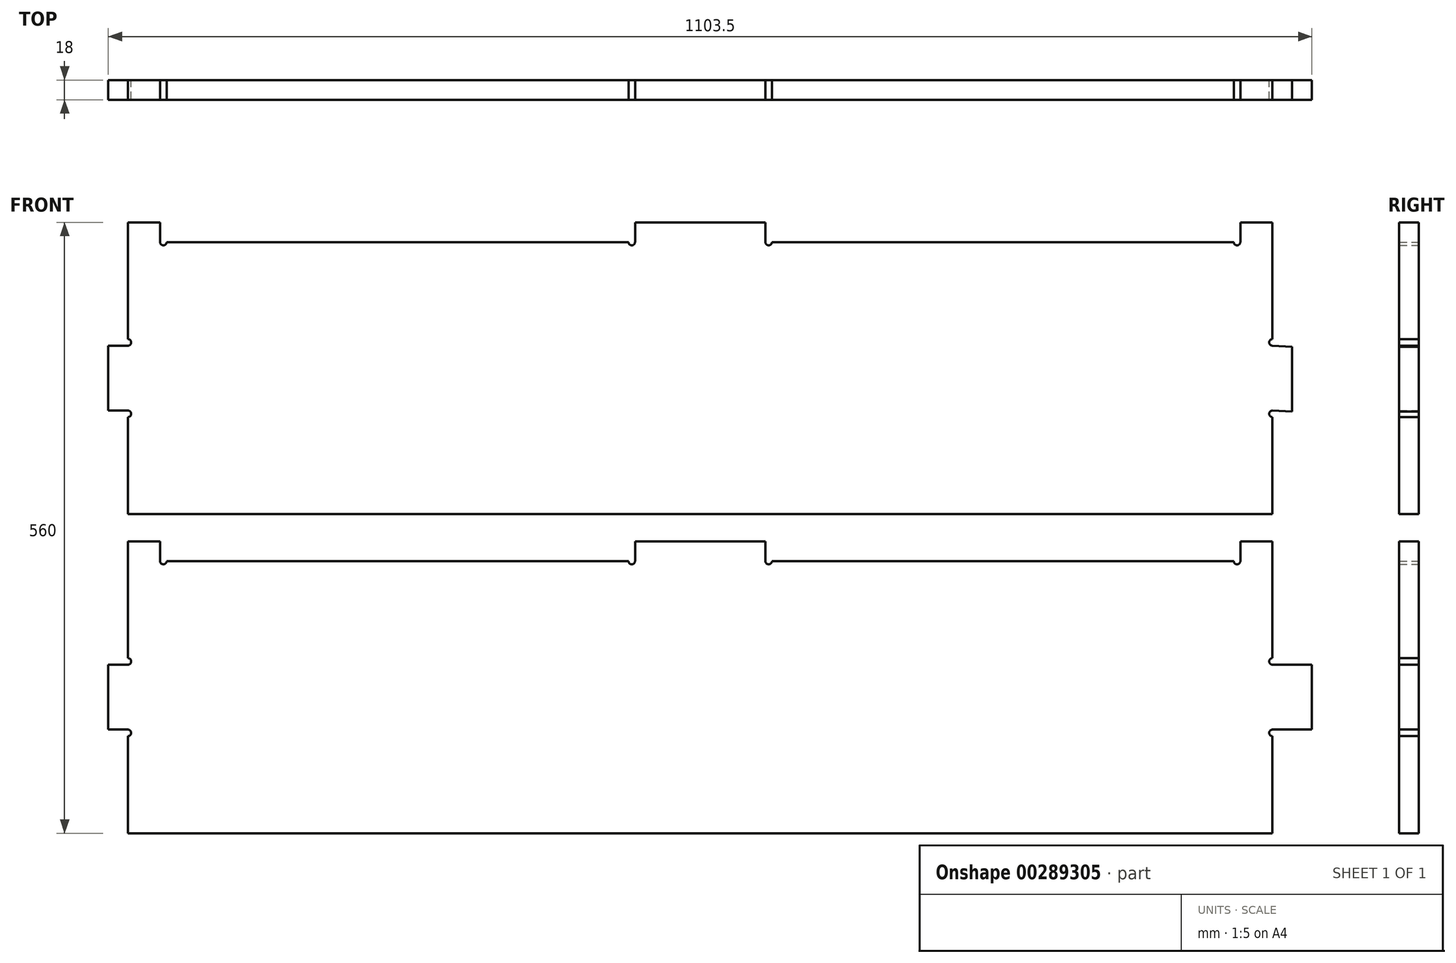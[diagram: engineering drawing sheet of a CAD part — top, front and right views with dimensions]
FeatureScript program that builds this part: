
annotation { "Feature Type Name" : "Feature", "Feature Type Description" : "" }
export const myFeature = defineFeature(function(context is Context, id is Id, definition is map)
    precondition{}
    {
        {
            var Q0;
            Q0=qCreatedBy(makeId("Front.planeOp"),FACE);
            var sketch = newSketch(context, id + "F0", { "sketchPlane" : qUnion([Q0])});
            skLineSegment(sketch, "E0", {"start": v(-59.75, -882.5) * mm, "end": v(-59.75, -900.5) * mm});
            skArc(sketch, "E1", {"start": v(-59.75, -900.5) * mm, "mid": v(-62.76, -903.5) * mm, "end": v(-65.77, -900.5) * mm});
            skLineSegment(sketch, "E2", {"start": v(-65.77, -900.5) * mm, "end": v(-489.23, -900.5) * mm});
            skArc(sketch, "E3", {"start": v(-489.23, -900.5) * mm, "mid": v(-492.24, -903.5) * mm, "end": v(-495.25, -900.5) * mm});
            skLineSegment(sketch, "E4", {"start": v(-495.25, -900.5) * mm, "end": v(-495.25, -882.5) * mm});
            skLineSegment(sketch, "E5", {"start": v(-495.25, -882.5) * mm, "end": v(-524.75, -882.5) * mm});
            skLineSegment(sketch, "E6", {"start": v(-524.75, -882.5) * mm, "end": v(-524.75, -989.48) * mm});
            skArc(sketch, "E7", {"start": v(-524.75, -989.48) * mm, "mid": v(-521.74, -992.49) * mm, "end": v(-524.75, -995.5) * mm});
            skLineSegment(sketch, "E8", {"start": v(-524.75, -995.5) * mm, "end": v(-542.75, -995.5) * mm});
            skLineSegment(sketch, "E9", {"start": v(-542.75, -995.5) * mm, "end": v(-542.75, -1055) * mm});
            skLineSegment(sketch, "E10", {"start": v(-542.75, -1055) * mm, "end": v(-524.75, -1055) * mm});
            skArc(sketch, "E11", {"start": v(-524.75, -1055) * mm, "mid": v(-521.74, -1058) * mm, "end": v(-524.75, -1061.02) * mm});
            skLineSegment(sketch, "E12", {"start": v(-524.75, -1061.02) * mm, "end": v(-524.75, -1150) * mm});
            skLineSegment(sketch, "E13", {"start": v(-524.75, -1150) * mm, "end": v(524.75, -1150) * mm});
            skLineSegment(sketch, "E14", {"start": v(524.75, -1150) * mm, "end": v(524.75, -1061.02) * mm});
            skArc(sketch, "E15", {"start": v(524.75, -1061.02) * mm, "mid": v(521.74, -1058) * mm, "end": v(524.75, -1055) * mm});
            skLineSegment(sketch, "E16", {"start": v(524.75, -1055) * mm, "end": v(560.75, -1055) * mm});
            skLineSegment(sketch, "E17", {"start": v(560.75, -1055) * mm, "end": v(560.75, -995.5) * mm});
            skLineSegment(sketch, "E18", {"start": v(560.75, -995.5) * mm, "end": v(524.75, -995.5) * mm});
            skArc(sketch, "E19", {"start": v(524.75, -995.5) * mm, "mid": v(521.74, -992.49) * mm, "end": v(524.75, -989.48) * mm});
            skLineSegment(sketch, "E20", {"start": v(524.75, -989.48) * mm, "end": v(524.75, -882.5) * mm});
            skLineSegment(sketch, "E21", {"start": v(524.75, -882.5) * mm, "end": v(495.25, -882.5) * mm});
            skLineSegment(sketch, "E22", {"start": v(495.25, -882.5) * mm, "end": v(495.25, -900.5) * mm});
            skArc(sketch, "E23", {"start": v(495.25, -900.5) * mm, "mid": v(492.24, -903.5) * mm, "end": v(489.23, -900.5) * mm});
            skLineSegment(sketch, "E24", {"start": v(489.23, -900.5) * mm, "end": v(65.77, -900.5) * mm});
            skArc(sketch, "E25", {"start": v(65.77, -900.5) * mm, "mid": v(62.76, -903.5) * mm, "end": v(59.75, -900.5) * mm});
            skLineSegment(sketch, "E26", {"start": v(59.75, -900.5) * mm, "end": v(59.75, -882.5) * mm});
            skLineSegment(sketch, "E27", {"start": v(59.75, -882.5) * mm, "end": v(-59.75, -882.5) * mm});
            skLineSegment(sketch, "E28", {"start": v(-59.75, -590) * mm, "end": v(-59.75, -608) * mm});
            skArc(sketch, "E29", {"start": v(-59.75, -608) * mm, "mid": v(-62.76, -611) * mm, "end": v(-65.77, -608) * mm});
            skLineSegment(sketch, "E30", {"start": v(-65.77, -608) * mm, "end": v(-489.23, -608) * mm});
            skArc(sketch, "E31", {"start": v(-489.23, -608) * mm, "mid": v(-492.24, -611) * mm, "end": v(-495.25, -608) * mm});
            skLineSegment(sketch, "E32", {"start": v(-495.25, -608) * mm, "end": v(-495.25, -590) * mm});
            skLineSegment(sketch, "E33", {"start": v(-495.25, -590) * mm, "end": v(-524.75, -590) * mm});
            skLineSegment(sketch, "E34", {"start": v(-524.75, -590) * mm, "end": v(-524.75, -696.98) * mm});
            skArc(sketch, "E35", {"start": v(-524.75, -696.98) * mm, "mid": v(-521.74, -699.99) * mm, "end": v(-524.75, -703) * mm});
            skLineSegment(sketch, "E36", {"start": v(-524.75, -703) * mm, "end": v(-542.75, -703) * mm});
            skLineSegment(sketch, "E37", {"start": v(-542.75, -703) * mm, "end": v(-542.75, -762.5) * mm});
            skLineSegment(sketch, "E38", {"start": v(-542.75, -762.5) * mm, "end": v(-524.75, -762.5) * mm});
            skArc(sketch, "E39", {"start": v(-524.75, -762.5) * mm, "mid": v(-521.74, -765.5) * mm, "end": v(-524.75, -768.52) * mm});
            skLineSegment(sketch, "E40", {"start": v(-524.75, -768.52) * mm, "end": v(-524.75, -857.5) * mm});
            skLineSegment(sketch, "E41", {"start": v(-524.75, -857.5) * mm, "end": v(524.75, -857.5) * mm});
            skLineSegment(sketch, "E42", {"start": v(524.75, -857.5) * mm, "end": v(524.75, -768.52) * mm});
            skArc(sketch, "E43", {"start": v(524.75, -768.52) * mm, "mid": v(521.74, -765.5) * mm, "end": v(524.75, -762.5) * mm});
            skLineSegment(sketch, "E44", {"start": v(524.75, -762.5) * mm, "end": v(542.77, -763.42) * mm});
            skLineSegment(sketch, "E45", {"start": v(542.77, -763.42) * mm, "end": v(542.77, -703.92) * mm});
            skLineSegment(sketch, "E46", {"start": v(542.77, -703.92) * mm, "end": v(524.75, -703) * mm});
            skArc(sketch, "E47", {"start": v(524.75, -703) * mm, "mid": v(521.74, -699.99) * mm, "end": v(524.75, -696.98) * mm});
            skLineSegment(sketch, "E48", {"start": v(524.75, -696.98) * mm, "end": v(524.75, -590) * mm});
            skLineSegment(sketch, "E49", {"start": v(524.75, -590) * mm, "end": v(495.25, -590) * mm});
            skLineSegment(sketch, "E50", {"start": v(495.25, -590) * mm, "end": v(495.25, -608) * mm});
            skArc(sketch, "E51", {"start": v(495.25, -608) * mm, "mid": v(492.24, -611) * mm, "end": v(489.23, -608) * mm});
            skLineSegment(sketch, "E52", {"start": v(489.23, -608) * mm, "end": v(65.77, -608) * mm});
            skArc(sketch, "E53", {"start": v(65.77, -608) * mm, "mid": v(62.76, -611) * mm, "end": v(59.75, -608) * mm});
            skLineSegment(sketch, "E54", {"start": v(59.75, -608) * mm, "end": v(59.75, -590) * mm});
            skLineSegment(sketch, "E55", {"start": v(59.75, -590) * mm, "end": v(-59.75, -590) * mm});
            skLineSegment(sketch, "E56", {"start": v(-59.75, -297.5) * mm, "end": v(-59.75, -315.5) * mm});
            skArc(sketch, "E57", {"start": v(-59.75, -315.5) * mm, "mid": v(-62.76, -318.5) * mm, "end": v(-65.77, -315.5) * mm});
            skLineSegment(sketch, "E58", {"start": v(-65.77, -315.5) * mm, "end": v(-489.23, -315.5) * mm});
            skArc(sketch, "E59", {"start": v(-489.23, -315.5) * mm, "mid": v(-492.24, -318.5) * mm, "end": v(-495.25, -315.5) * mm});
            skLineSegment(sketch, "E60", {"start": v(-495.25, -315.5) * mm, "end": v(-495.25, -297.5) * mm});
            skLineSegment(sketch, "E61", {"start": v(-495.25, -297.5) * mm, "end": v(-524.75, -297.5) * mm});
            skLineSegment(sketch, "E62", {"start": v(-524.75, -297.5) * mm, "end": v(-524.75, -404.48) * mm});
            skArc(sketch, "E63", {"start": v(-524.75, -404.48) * mm, "mid": v(-521.74, -407.49) * mm, "end": v(-524.75, -410.5) * mm});
            skLineSegment(sketch, "E64", {"start": v(-524.75, -410.5) * mm, "end": v(-542.75, -410.5) * mm});
            skLineSegment(sketch, "E65", {"start": v(-542.75, -410.5) * mm, "end": v(-542.75, -470) * mm});
            skLineSegment(sketch, "E66", {"start": v(-542.75, -470) * mm, "end": v(-524.75, -470) * mm});
            skArc(sketch, "E67", {"start": v(-524.75, -470) * mm, "mid": v(-521.74, -473) * mm, "end": v(-524.75, -476.02) * mm});
            skLineSegment(sketch, "E68", {"start": v(-524.75, -476.02) * mm, "end": v(-524.75, -565) * mm});
            skLineSegment(sketch, "E69", {"start": v(-524.75, -565) * mm, "end": v(524.75, -565) * mm});
            skLineSegment(sketch, "E70", {"start": v(524.75, -565) * mm, "end": v(524.75, -476.02) * mm});
            skArc(sketch, "E71", {"start": v(524.75, -476.02) * mm, "mid": v(521.74, -473) * mm, "end": v(524.75, -470) * mm});
            skLineSegment(sketch, "E72", {"start": v(524.75, -470) * mm, "end": v(542.77, -470.92) * mm});
            skLineSegment(sketch, "E73", {"start": v(542.77, -470.92) * mm, "end": v(542.77, -411.42) * mm});
            skLineSegment(sketch, "E74", {"start": v(542.77, -411.42) * mm, "end": v(524.75, -410.5) * mm});
            skArc(sketch, "E75", {"start": v(524.75, -410.5) * mm, "mid": v(521.74, -407.49) * mm, "end": v(524.75, -404.48) * mm});
            skLineSegment(sketch, "E76", {"start": v(524.75, -404.48) * mm, "end": v(524.75, -297.5) * mm});
            skLineSegment(sketch, "E77", {"start": v(524.75, -297.5) * mm, "end": v(495.25, -297.5) * mm});
            skLineSegment(sketch, "E78", {"start": v(495.25, -297.5) * mm, "end": v(495.25, -315.5) * mm});
            skArc(sketch, "E79", {"start": v(495.25, -315.5) * mm, "mid": v(492.24, -318.5) * mm, "end": v(489.23, -315.5) * mm});
            skLineSegment(sketch, "E80", {"start": v(489.23, -315.5) * mm, "end": v(65.77, -315.5) * mm});
            skArc(sketch, "E81", {"start": v(65.77, -315.5) * mm, "mid": v(62.76, -318.5) * mm, "end": v(59.75, -315.5) * mm});
            skLineSegment(sketch, "E82", {"start": v(59.75, -315.5) * mm, "end": v(59.75, -297.5) * mm});
            skLineSegment(sketch, "E83", {"start": v(59.75, -297.5) * mm, "end": v(-59.75, -297.5) * mm});
            skLineSegment(sketch, "E84", {"start": v(-59.75, -5) * mm, "end": v(-59.75, -23) * mm});
            skArc(sketch, "E85", {"start": v(-59.75, -23) * mm, "mid": v(-62.76, -26) * mm, "end": v(-65.77, -23) * mm});
            skLineSegment(sketch, "E86", {"start": v(-65.77, -23) * mm, "end": v(-489.23, -23) * mm});
            skArc(sketch, "E87", {"start": v(-489.23, -23) * mm, "mid": v(-492.24, -26) * mm, "end": v(-495.25, -23) * mm});
            skLineSegment(sketch, "E88", {"start": v(-495.25, -23) * mm, "end": v(-495.25, -5) * mm});
            skLineSegment(sketch, "E89", {"start": v(-495.25, -5) * mm, "end": v(-524.75, -5) * mm});
            skLineSegment(sketch, "E90", {"start": v(-524.75, -5) * mm, "end": v(-524.75, -111.98) * mm});
            skArc(sketch, "E91", {"start": v(-524.75, -111.98) * mm, "mid": v(-521.74, -114.99) * mm, "end": v(-524.75, -118) * mm});
            skLineSegment(sketch, "E92", {"start": v(-524.75, -118) * mm, "end": v(-542.75, -118) * mm});
            skLineSegment(sketch, "E93", {"start": v(-542.75, -118) * mm, "end": v(-542.75, -177.5) * mm});
            skLineSegment(sketch, "E94", {"start": v(-542.75, -177.5) * mm, "end": v(-524.75, -177.5) * mm});
            skArc(sketch, "E95", {"start": v(-524.75, -177.5) * mm, "mid": v(-521.74, -180.5) * mm, "end": v(-524.75, -183.52) * mm});
            skLineSegment(sketch, "E96", {"start": v(-524.75, -183.52) * mm, "end": v(-524.75, -272.5) * mm});
            skLineSegment(sketch, "E97", {"start": v(-524.75, -272.5) * mm, "end": v(524.75, -272.5) * mm});
            skLineSegment(sketch, "E98", {"start": v(524.75, -272.5) * mm, "end": v(524.75, -183.52) * mm});
            skArc(sketch, "E99", {"start": v(524.75, -183.52) * mm, "mid": v(521.74, -180.5) * mm, "end": v(524.75, -177.5) * mm});
            skLineSegment(sketch, "E100", {"start": v(524.75, -177.5) * mm, "end": v(542.77, -178.42) * mm});
            skLineSegment(sketch, "E101", {"start": v(542.77, -178.42) * mm, "end": v(542.77, -118.92) * mm});
            skLineSegment(sketch, "E102", {"start": v(542.77, -118.92) * mm, "end": v(524.75, -118) * mm});
            skArc(sketch, "E103", {"start": v(524.75, -118) * mm, "mid": v(521.74, -114.99) * mm, "end": v(524.75, -111.98) * mm});
            skLineSegment(sketch, "E104", {"start": v(524.75, -111.98) * mm, "end": v(524.75, -5) * mm});
            skLineSegment(sketch, "E105", {"start": v(524.75, -5) * mm, "end": v(495.25, -5) * mm});
            skLineSegment(sketch, "E106", {"start": v(495.25, -5) * mm, "end": v(495.25, -23) * mm});
            skArc(sketch, "E107", {"start": v(495.25, -23) * mm, "mid": v(492.24, -26) * mm, "end": v(489.23, -23) * mm});
            skLineSegment(sketch, "E108", {"start": v(489.23, -23) * mm, "end": v(65.77, -23) * mm});
            skArc(sketch, "E109", {"start": v(65.77, -23) * mm, "mid": v(62.76, -26) * mm, "end": v(59.75, -23) * mm});
            skLineSegment(sketch, "E110", {"start": v(59.75, -23) * mm, "end": v(59.75, -5) * mm});
            skLineSegment(sketch, "E111", {"start": v(59.75, -5) * mm, "end": v(-59.75, -5) * mm});
            skLineSegment(sketch, "E112", {"start": v(-59.75, 287.5) * mm, "end": v(-59.75, 269.5) * mm});
            skArc(sketch, "E113", {"start": v(-59.75, 269.5) * mm, "mid": v(-62.76, 266.5) * mm, "end": v(-65.77, 269.5) * mm});
            skLineSegment(sketch, "E114", {"start": v(-65.77, 269.5) * mm, "end": v(-489.23, 269.5) * mm});
            skArc(sketch, "E115", {"start": v(-489.23, 269.5) * mm, "mid": v(-492.24, 266.5) * mm, "end": v(-495.25, 269.5) * mm});
            skLineSegment(sketch, "E116", {"start": v(-495.25, 269.5) * mm, "end": v(-495.25, 287.5) * mm});
            skLineSegment(sketch, "E117", {"start": v(-495.25, 287.5) * mm, "end": v(-524.75, 287.5) * mm});
            skLineSegment(sketch, "E118", {"start": v(-524.75, 287.5) * mm, "end": v(-524.75, 180.52) * mm});
            skArc(sketch, "E119", {"start": v(-524.75, 180.52) * mm, "mid": v(-521.74, 177.51) * mm, "end": v(-524.75, 174.5) * mm});
            skLineSegment(sketch, "E120", {"start": v(-524.75, 174.5) * mm, "end": v(-542.75, 174.5) * mm});
            skLineSegment(sketch, "E121", {"start": v(-542.75, 174.5) * mm, "end": v(-542.75, 115) * mm});
            skLineSegment(sketch, "E122", {"start": v(-542.75, 115) * mm, "end": v(-524.75, 115) * mm});
            skArc(sketch, "E123", {"start": v(-524.75, 115) * mm, "mid": v(-521.74, 112) * mm, "end": v(-524.75, 108.98) * mm});
            skLineSegment(sketch, "E124", {"start": v(-524.75, 108.98) * mm, "end": v(-524.75, 20) * mm});
            skLineSegment(sketch, "E125", {"start": v(-524.75, 20) * mm, "end": v(524.75, 20) * mm});
            skLineSegment(sketch, "E126", {"start": v(524.75, 20) * mm, "end": v(524.75, 108.98) * mm});
            skArc(sketch, "E127", {"start": v(524.75, 108.98) * mm, "mid": v(521.74, 112) * mm, "end": v(524.75, 115) * mm});
            skLineSegment(sketch, "E128", {"start": v(524.75, 115) * mm, "end": v(542.77, 114.08) * mm});
            skLineSegment(sketch, "E129", {"start": v(542.77, 114.08) * mm, "end": v(542.77, 173.58) * mm});
            skLineSegment(sketch, "E130", {"start": v(542.77, 173.58) * mm, "end": v(524.75, 174.5) * mm});
            skArc(sketch, "E131", {"start": v(524.75, 174.5) * mm, "mid": v(521.74, 177.51) * mm, "end": v(524.75, 180.52) * mm});
            skLineSegment(sketch, "E132", {"start": v(524.75, 180.52) * mm, "end": v(524.75, 287.5) * mm});
            skLineSegment(sketch, "E133", {"start": v(524.75, 287.5) * mm, "end": v(495.25, 287.5) * mm});
            skLineSegment(sketch, "E134", {"start": v(495.25, 287.5) * mm, "end": v(495.25, 269.5) * mm});
            skArc(sketch, "E135", {"start": v(495.25, 269.5) * mm, "mid": v(492.24, 266.5) * mm, "end": v(489.23, 269.5) * mm});
            skLineSegment(sketch, "E136", {"start": v(489.23, 269.5) * mm, "end": v(65.77, 269.5) * mm});
            skArc(sketch, "E137", {"start": v(65.77, 269.5) * mm, "mid": v(62.76, 266.5) * mm, "end": v(59.75, 269.5) * mm});
            skLineSegment(sketch, "E138", {"start": v(59.75, 269.5) * mm, "end": v(59.75, 287.5) * mm});
            skLineSegment(sketch, "E139", {"start": v(59.75, 287.5) * mm, "end": v(-59.75, 287.5) * mm});
            skLineSegment(sketch, "E140", {"start": v(-59.75, 580) * mm, "end": v(-59.75, 562) * mm});
            skArc(sketch, "E141", {"start": v(-59.75, 562) * mm, "mid": v(-62.76, 559) * mm, "end": v(-65.77, 562) * mm});
            skLineSegment(sketch, "E142", {"start": v(-65.77, 562) * mm, "end": v(-489.23, 562) * mm});
            skArc(sketch, "E143", {"start": v(-489.23, 562) * mm, "mid": v(-492.24, 559) * mm, "end": v(-495.25, 562) * mm});
            skLineSegment(sketch, "E144", {"start": v(-495.25, 562) * mm, "end": v(-495.25, 580) * mm});
            skLineSegment(sketch, "E145", {"start": v(-495.25, 580) * mm, "end": v(-524.75, 580) * mm});
            skLineSegment(sketch, "E146", {"start": v(-524.75, 580) * mm, "end": v(-524.75, 473.02) * mm});
            skArc(sketch, "E147", {"start": v(-524.75, 473.02) * mm, "mid": v(-521.74, 470.01) * mm, "end": v(-524.75, 467) * mm});
            skLineSegment(sketch, "E148", {"start": v(-524.75, 467) * mm, "end": v(-542.75, 467) * mm});
            skLineSegment(sketch, "E149", {"start": v(-542.75, 467) * mm, "end": v(-542.75, 407.5) * mm});
            skLineSegment(sketch, "E150", {"start": v(-542.75, 407.5) * mm, "end": v(-524.75, 407.5) * mm});
            skArc(sketch, "E151", {"start": v(-524.75, 407.5) * mm, "mid": v(-521.74, 404.5) * mm, "end": v(-524.75, 401.48) * mm});
            skLineSegment(sketch, "E152", {"start": v(-524.75, 401.48) * mm, "end": v(-524.75, 312.5) * mm});
            skLineSegment(sketch, "E153", {"start": v(-524.75, 312.5) * mm, "end": v(524.75, 312.5) * mm});
            skLineSegment(sketch, "E154", {"start": v(524.75, 312.5) * mm, "end": v(524.75, 401.48) * mm});
            skArc(sketch, "E155", {"start": v(524.75, 401.48) * mm, "mid": v(521.74, 404.5) * mm, "end": v(524.75, 407.5) * mm});
            skLineSegment(sketch, "E156", {"start": v(524.75, 407.5) * mm, "end": v(542.77, 406.58) * mm});
            skLineSegment(sketch, "E157", {"start": v(542.77, 406.58) * mm, "end": v(542.77, 466.08) * mm});
            skLineSegment(sketch, "E158", {"start": v(542.77, 466.08) * mm, "end": v(524.75, 467) * mm});
            skArc(sketch, "E159", {"start": v(524.75, 467) * mm, "mid": v(521.74, 470.01) * mm, "end": v(524.75, 473.02) * mm});
            skLineSegment(sketch, "E160", {"start": v(524.75, 473.02) * mm, "end": v(524.75, 580) * mm});
            skLineSegment(sketch, "E161", {"start": v(524.75, 580) * mm, "end": v(495.25, 580) * mm});
            skLineSegment(sketch, "E162", {"start": v(495.25, 580) * mm, "end": v(495.25, 562) * mm});
            skArc(sketch, "E163", {"start": v(495.25, 562) * mm, "mid": v(492.24, 559) * mm, "end": v(489.23, 562) * mm});
            skLineSegment(sketch, "E164", {"start": v(489.23, 562) * mm, "end": v(65.77, 562) * mm});
            skArc(sketch, "E165", {"start": v(65.77, 562) * mm, "mid": v(62.76, 559) * mm, "end": v(59.75, 562) * mm});
            skLineSegment(sketch, "E166", {"start": v(59.75, 562) * mm, "end": v(59.75, 580) * mm});
            skLineSegment(sketch, "E167", {"start": v(59.75, 580) * mm, "end": v(-59.75, 580) * mm});
            skLineSegment(sketch, "E168", {"start": v(-59.75, 872.5) * mm, "end": v(-59.75, 854.5) * mm});
            skArc(sketch, "E169", {"start": v(-59.75, 854.5) * mm, "mid": v(-62.76, 851.5) * mm, "end": v(-65.77, 854.5) * mm});
            skLineSegment(sketch, "E170", {"start": v(-65.77, 854.5) * mm, "end": v(-489.23, 854.5) * mm});
            skArc(sketch, "E171", {"start": v(-489.23, 854.5) * mm, "mid": v(-492.24, 851.5) * mm, "end": v(-495.25, 854.5) * mm});
            skLineSegment(sketch, "E172", {"start": v(-495.25, 854.5) * mm, "end": v(-495.25, 872.5) * mm});
            skLineSegment(sketch, "E173", {"start": v(-495.25, 872.5) * mm, "end": v(-524.75, 872.5) * mm});
            skLineSegment(sketch, "E174", {"start": v(-524.75, 872.5) * mm, "end": v(-524.75, 765.52) * mm});
            skArc(sketch, "E175", {"start": v(-524.75, 765.52) * mm, "mid": v(-521.74, 762.51) * mm, "end": v(-524.75, 759.5) * mm});
            skLineSegment(sketch, "E176", {"start": v(-524.75, 759.5) * mm, "end": v(-542.75, 759.5) * mm});
            skLineSegment(sketch, "E177", {"start": v(-542.75, 759.5) * mm, "end": v(-542.75, 700) * mm});
            skLineSegment(sketch, "E178", {"start": v(-542.75, 700) * mm, "end": v(-524.75, 700) * mm});
            skArc(sketch, "E179", {"start": v(-524.75, 700) * mm, "mid": v(-521.74, 697) * mm, "end": v(-524.75, 693.98) * mm});
            skLineSegment(sketch, "E180", {"start": v(-524.75, 693.98) * mm, "end": v(-524.75, 605) * mm});
            skLineSegment(sketch, "E181", {"start": v(-524.75, 605) * mm, "end": v(524.75, 605) * mm});
            skLineSegment(sketch, "E182", {"start": v(524.75, 605) * mm, "end": v(524.75, 693.98) * mm});
            skArc(sketch, "E183", {"start": v(524.75, 693.98) * mm, "mid": v(521.74, 697) * mm, "end": v(524.75, 700) * mm});
            skLineSegment(sketch, "E184", {"start": v(524.75, 700) * mm, "end": v(542.77, 699.08) * mm});
            skLineSegment(sketch, "E185", {"start": v(542.77, 699.08) * mm, "end": v(542.77, 758.58) * mm});
            skLineSegment(sketch, "E186", {"start": v(542.77, 758.58) * mm, "end": v(524.75, 759.5) * mm});
            skArc(sketch, "E187", {"start": v(524.75, 759.5) * mm, "mid": v(521.74, 762.51) * mm, "end": v(524.75, 765.52) * mm});
            skLineSegment(sketch, "E188", {"start": v(524.75, 765.52) * mm, "end": v(524.75, 872.5) * mm});
            skLineSegment(sketch, "E189", {"start": v(524.75, 872.5) * mm, "end": v(495.25, 872.5) * mm});
            skLineSegment(sketch, "E190", {"start": v(495.25, 872.5) * mm, "end": v(495.25, 854.5) * mm});
            skArc(sketch, "E191", {"start": v(495.25, 854.5) * mm, "mid": v(492.24, 851.5) * mm, "end": v(489.23, 854.5) * mm});
            skLineSegment(sketch, "E192", {"start": v(489.23, 854.5) * mm, "end": v(65.77, 854.5) * mm});
            skArc(sketch, "E193", {"start": v(65.77, 854.5) * mm, "mid": v(62.76, 851.5) * mm, "end": v(59.75, 854.5) * mm});
            skLineSegment(sketch, "E194", {"start": v(59.75, 854.5) * mm, "end": v(59.75, 872.5) * mm});
            skLineSegment(sketch, "E195", {"start": v(59.75, 872.5) * mm, "end": v(-59.75, 872.5) * mm});
            skLineSegment(sketch, "E196", {"start": v(-59.75, 1165) * mm, "end": v(-59.75, 1147) * mm});
            skArc(sketch, "E197", {"start": v(-59.75, 1147) * mm, "mid": v(-62.76, 1144) * mm, "end": v(-65.77, 1147) * mm});
            skLineSegment(sketch, "E198", {"start": v(-65.77, 1147) * mm, "end": v(-489.23, 1147) * mm});
            skArc(sketch, "E199", {"start": v(-489.23, 1147) * mm, "mid": v(-492.24, 1144) * mm, "end": v(-495.25, 1147) * mm});
            skLineSegment(sketch, "E200", {"start": v(-495.25, 1147) * mm, "end": v(-495.25, 1165) * mm});
            skLineSegment(sketch, "E201", {"start": v(-495.25, 1165) * mm, "end": v(-524.75, 1165) * mm});
            skLineSegment(sketch, "E202", {"start": v(-524.75, 1165) * mm, "end": v(-524.75, 1058.02) * mm});
            skArc(sketch, "E203", {"start": v(-524.75, 1058.02) * mm, "mid": v(-521.74, 1055.01) * mm, "end": v(-524.75, 1052) * mm});
            skLineSegment(sketch, "E204", {"start": v(-524.75, 1052) * mm, "end": v(-542.75, 1052) * mm});
            skLineSegment(sketch, "E205", {"start": v(-542.75, 1052) * mm, "end": v(-542.75, 992.5) * mm});
            skLineSegment(sketch, "E206", {"start": v(-542.75, 992.5) * mm, "end": v(-524.75, 992.5) * mm});
            skArc(sketch, "E207", {"start": v(-524.75, 992.5) * mm, "mid": v(-521.74, 989.5) * mm, "end": v(-524.75, 986.48) * mm});
            skLineSegment(sketch, "E208", {"start": v(-524.75, 986.48) * mm, "end": v(-524.75, 897.5) * mm});
            skLineSegment(sketch, "E209", {"start": v(-524.75, 897.5) * mm, "end": v(524.75, 897.5) * mm});
            skLineSegment(sketch, "E210", {"start": v(524.75, 897.5) * mm, "end": v(524.75, 986.48) * mm});
            skArc(sketch, "E211", {"start": v(524.75, 986.48) * mm, "mid": v(521.74, 989.5) * mm, "end": v(524.75, 992.5) * mm});
            skLineSegment(sketch, "E212", {"start": v(524.75, 992.5) * mm, "end": v(542.77, 991.58) * mm});
            skLineSegment(sketch, "E213", {"start": v(542.77, 991.58) * mm, "end": v(542.77, 1051.08) * mm});
            skLineSegment(sketch, "E214", {"start": v(542.77, 1051.08) * mm, "end": v(524.75, 1052) * mm});
            skArc(sketch, "E215", {"start": v(524.75, 1052) * mm, "mid": v(521.74, 1055.01) * mm, "end": v(524.75, 1058.02) * mm});
            skLineSegment(sketch, "E216", {"start": v(524.75, 1058.02) * mm, "end": v(524.75, 1165) * mm});
            skLineSegment(sketch, "E217", {"start": v(524.75, 1165) * mm, "end": v(495.25, 1165) * mm});
            skLineSegment(sketch, "E218", {"start": v(495.25, 1165) * mm, "end": v(495.25, 1147) * mm});
            skArc(sketch, "E219", {"start": v(495.25, 1147) * mm, "mid": v(492.24, 1144) * mm, "end": v(489.23, 1147) * mm});
            skLineSegment(sketch, "E220", {"start": v(489.23, 1147) * mm, "end": v(65.77, 1147) * mm});
            skArc(sketch, "E221", {"start": v(65.77, 1147) * mm, "mid": v(62.76, 1144) * mm, "end": v(59.75, 1147) * mm});
            skLineSegment(sketch, "E222", {"start": v(59.75, 1147) * mm, "end": v(59.75, 1165) * mm});
            skLineSegment(sketch, "E223", {"start": v(59.75, 1165) * mm, "end": v(-59.75, 1165) * mm});
            skArc(sketch, "E224", {"start": v(-561.12, 1112.28) * mm, "mid": v(-563.77, 1111.18) * mm, "end": v(-564.87, 1108.53) * mm});
            skArc(sketch, "E225", {"start": v(-564.87, 1108.53) * mm, "mid": v(-563.77, 1105.88) * mm, "end": v(-561.12, 1104.78) * mm});
            skArc(sketch, "E226", {"start": v(-561.12, 1104.78) * mm, "mid": v(-558.47, 1105.88) * mm, "end": v(-557.37, 1108.53) * mm});
            skArc(sketch, "E227", {"start": v(-557.37, 1108.53) * mm, "mid": v(-558.47, 1111.18) * mm, "end": v(-561.12, 1112.28) * mm});
            skArc(sketch, "E228", {"start": v(-558.37, 671.4) * mm, "mid": v(-561.02, 670.3) * mm, "end": v(-562.12, 667.66) * mm});
            skArc(sketch, "E229", {"start": v(-562.12, 667.66) * mm, "mid": v(-561.02, 665) * mm, "end": v(-558.37, 663.9) * mm});
            skArc(sketch, "E230", {"start": v(-558.37, 663.9) * mm, "mid": v(-555.72, 665) * mm, "end": v(-554.62, 667.66) * mm});
            skArc(sketch, "E231", {"start": v(-554.62, 667.66) * mm, "mid": v(-555.72, 670.3) * mm, "end": v(-558.37, 671.4) * mm});
            skArc(sketch, "E232", {"start": v(-560.3, 84.95) * mm, "mid": v(-562.94, 83.85) * mm, "end": v(-564.04, 81.2) * mm});
            skArc(sketch, "E233", {"start": v(-564.04, 81.2) * mm, "mid": v(-562.94, 78.55) * mm, "end": v(-560.3, 77.45) * mm});
            skArc(sketch, "E234", {"start": v(-560.3, 77.45) * mm, "mid": v(-557.64, 78.55) * mm, "end": v(-556.54, 81.2) * mm});
            skArc(sketch, "E235", {"start": v(-556.54, 81.2) * mm, "mid": v(-557.64, 83.85) * mm, "end": v(-560.3, 84.95) * mm});
            skArc(sketch, "E236", {"start": v(-560.3, -509.2) * mm, "mid": v(-562.94, -510.3) * mm, "end": v(-564.04, -512.95) * mm});
            skArc(sketch, "E237", {"start": v(-564.04, -512.95) * mm, "mid": v(-562.94, -515.6) * mm, "end": v(-560.3, -516.7) * mm});
            skArc(sketch, "E238", {"start": v(-560.3, -516.7) * mm, "mid": v(-557.64, -515.6) * mm, "end": v(-556.54, -512.95) * mm});
            skArc(sketch, "E239", {"start": v(-556.54, -512.95) * mm, "mid": v(-557.64, -510.3) * mm, "end": v(-560.3, -509.2) * mm});
            skArc(sketch, "E240", {"start": v(-558.37, -959.13) * mm, "mid": v(-561.02, -960.23) * mm, "end": v(-562.12, -962.88) * mm});
            skArc(sketch, "E241", {"start": v(-562.12, -962.88) * mm, "mid": v(-561.02, -965.54) * mm, "end": v(-558.37, -966.63) * mm});
            skArc(sketch, "E242", {"start": v(-558.37, -966.63) * mm, "mid": v(-555.72, -965.54) * mm, "end": v(-554.62, -962.88) * mm});
            skArc(sketch, "E243", {"start": v(-554.62, -962.88) * mm, "mid": v(-555.72, -960.23) * mm, "end": v(-558.37, -959.13) * mm});
            skArc(sketch, "E244", {"start": v(-283.4, -1170.16) * mm, "mid": v(-286.06, -1171.26) * mm, "end": v(-287.16, -1173.91) * mm});
            skArc(sketch, "E245", {"start": v(-287.16, -1173.91) * mm, "mid": v(-286.06, -1176.56) * mm, "end": v(-283.4, -1177.66) * mm});
            skArc(sketch, "E246", {"start": v(-283.4, -1177.66) * mm, "mid": v(-280.76, -1176.56) * mm, "end": v(-279.66, -1173.91) * mm});
            skArc(sketch, "E247", {"start": v(-279.66, -1173.91) * mm, "mid": v(-280.76, -1171.26) * mm, "end": v(-283.4, -1170.16) * mm});
            skArc(sketch, "E248", {"start": v(233.35, -1174.97) * mm, "mid": v(230.7, -1176.07) * mm, "end": v(229.6, -1178.72) * mm});
            skArc(sketch, "E249", {"start": v(229.6, -1178.72) * mm, "mid": v(230.7, -1181.37) * mm, "end": v(233.35, -1182.47) * mm});
            skArc(sketch, "E250", {"start": v(233.35, -1182.47) * mm, "mid": v(236, -1181.37) * mm, "end": v(237.1, -1178.72) * mm});
            skArc(sketch, "E251", {"start": v(237.1, -1178.72) * mm, "mid": v(236, -1176.07) * mm, "end": v(233.35, -1174.97) * mm});
            skArc(sketch, "E252", {"start": v(557.82, -949.04) * mm, "mid": v(555.17, -950.14) * mm, "end": v(554.07, -952.79) * mm});
            skArc(sketch, "E253", {"start": v(554.07, -952.79) * mm, "mid": v(555.17, -955.44) * mm, "end": v(557.82, -956.54) * mm});
            skArc(sketch, "E254", {"start": v(557.82, -956.54) * mm, "mid": v(560.47, -955.44) * mm, "end": v(561.57, -952.79) * mm});
            skArc(sketch, "E255", {"start": v(561.57, -952.79) * mm, "mid": v(560.47, -950.14) * mm, "end": v(557.82, -949.04) * mm});
            skArc(sketch, "E256", {"start": v(560.22, -499.58) * mm, "mid": v(557.57, -500.68) * mm, "end": v(556.47, -503.33) * mm});
            skArc(sketch, "E257", {"start": v(556.47, -503.33) * mm, "mid": v(557.57, -505.98) * mm, "end": v(560.22, -507.08) * mm});
            skArc(sketch, "E258", {"start": v(560.22, -507.08) * mm, "mid": v(562.87, -505.98) * mm, "end": v(563.97, -503.33) * mm});
            skArc(sketch, "E259", {"start": v(563.97, -503.33) * mm, "mid": v(562.87, -500.68) * mm, "end": v(560.22, -499.58) * mm});
            skArc(sketch, "E260", {"start": v(560.22, 84.47) * mm, "mid": v(557.57, 83.37) * mm, "end": v(556.47, 80.72) * mm});
            skArc(sketch, "E261", {"start": v(556.47, 80.72) * mm, "mid": v(557.57, 78.07) * mm, "end": v(560.22, 76.97) * mm});
            skArc(sketch, "E262", {"start": v(560.22, 76.97) * mm, "mid": v(562.87, 78.07) * mm, "end": v(563.97, 80.72) * mm});
            skArc(sketch, "E263", {"start": v(563.97, 80.72) * mm, "mid": v(562.87, 83.37) * mm, "end": v(560.22, 84.47) * mm});
            skArc(sketch, "E264", {"start": v(556.47, 674.39) * mm, "mid": v(553.82, 673.29) * mm, "end": v(552.72, 670.64) * mm});
            skArc(sketch, "E265", {"start": v(552.72, 670.64) * mm, "mid": v(553.82, 667.98) * mm, "end": v(556.47, 666.89) * mm});
            skArc(sketch, "E266", {"start": v(556.47, 666.89) * mm, "mid": v(559.12, 667.98) * mm, "end": v(560.22, 670.64) * mm});
            skArc(sketch, "E267", {"start": v(560.22, 670.64) * mm, "mid": v(559.12, 673.29) * mm, "end": v(556.47, 674.39) * mm});
            skArc(sketch, "E268", {"start": v(572.24, 1132.4) * mm, "mid": v(569.59, 1131.3) * mm, "end": v(568.5, 1128.65) * mm});
            skArc(sketch, "E269", {"start": v(568.5, 1128.65) * mm, "mid": v(569.59, 1126) * mm, "end": v(572.24, 1124.9) * mm});
            skArc(sketch, "E270", {"start": v(572.24, 1124.9) * mm, "mid": v(574.9, 1126) * mm, "end": v(576, 1128.65) * mm});
            skArc(sketch, "E271", {"start": v(576, 1128.65) * mm, "mid": v(574.9, 1131.3) * mm, "end": v(572.24, 1132.4) * mm});
            skArc(sketch, "E272", {"start": v(252.47, 1182.63) * mm, "mid": v(249.82, 1181.53) * mm, "end": v(248.72, 1178.88) * mm});
            skArc(sketch, "E273", {"start": v(248.72, 1178.88) * mm, "mid": v(249.82, 1176.23) * mm, "end": v(252.47, 1175.13) * mm});
            skArc(sketch, "E274", {"start": v(252.47, 1175.13) * mm, "mid": v(255.13, 1176.23) * mm, "end": v(256.22, 1178.88) * mm});
            skArc(sketch, "E275", {"start": v(256.22, 1178.88) * mm, "mid": v(255.13, 1181.53) * mm, "end": v(252.47, 1182.63) * mm});
            skArc(sketch, "E276", {"start": v(-240.75, 1181.64) * mm, "mid": v(-243.4, 1180.55) * mm, "end": v(-244.5, 1177.9) * mm});
            skArc(sketch, "E277", {"start": v(-244.5, 1177.9) * mm, "mid": v(-243.4, 1175.24) * mm, "end": v(-240.75, 1174.14) * mm});
            skArc(sketch, "E278", {"start": v(-240.75, 1174.14) * mm, "mid": v(-238.1, 1175.24) * mm, "end": v(-237, 1177.9) * mm});
            skArc(sketch, "E279", {"start": v(-237, 1177.9) * mm, "mid": v(-238.1, 1180.55) * mm, "end": v(-240.75, 1181.64) * mm});
            skArc(sketch, "E280", {"start": v(-87.44, 882.04) * mm, "mid": v(-90.1, 880.95) * mm, "end": v(-91.2, 878.3) * mm});
            skArc(sketch, "E281", {"start": v(-91.2, 878.3) * mm, "mid": v(-90.1, 875.64) * mm, "end": v(-87.44, 874.54) * mm});
            skArc(sketch, "E282", {"start": v(-87.44, 874.54) * mm, "mid": v(-84.79, 875.64) * mm, "end": v(-83.7, 878.3) * mm});
            skArc(sketch, "E283", {"start": v(-83.7, 878.3) * mm, "mid": v(-84.79, 880.95) * mm, "end": v(-87.44, 882.04) * mm});
            skArc(sketch, "E284", {"start": v(94.07, 586.78) * mm, "mid": v(91.42, 585.68) * mm, "end": v(90.32, 583.03) * mm});
            skArc(sketch, "E285", {"start": v(90.32, 583.03) * mm, "mid": v(91.42, 580.38) * mm, "end": v(94.07, 579.28) * mm});
            skArc(sketch, "E286", {"start": v(94.07, 579.28) * mm, "mid": v(96.72, 580.38) * mm, "end": v(97.82, 583.03) * mm});
            skArc(sketch, "E287", {"start": v(97.82, 583.03) * mm, "mid": v(96.72, 585.68) * mm, "end": v(94.07, 586.78) * mm});
            skArc(sketch, "E288", {"start": v(-96.67, 292.98) * mm, "mid": v(-99.32, 291.88) * mm, "end": v(-100.42, 289.23) * mm});
            skArc(sketch, "E289", {"start": v(-100.42, 289.23) * mm, "mid": v(-99.32, 286.58) * mm, "end": v(-96.67, 285.48) * mm});
            skArc(sketch, "E290", {"start": v(-96.67, 285.48) * mm, "mid": v(-94.02, 286.58) * mm, "end": v(-92.92, 289.23) * mm});
            skArc(sketch, "E291", {"start": v(-92.92, 289.23) * mm, "mid": v(-94.02, 291.88) * mm, "end": v(-96.67, 292.98) * mm});
            skArc(sketch, "E292", {"start": v(95.61, 0.34) * mm, "mid": v(92.96, -0.76) * mm, "end": v(91.86, -3.41) * mm});
            skArc(sketch, "E293", {"start": v(91.86, -3.41) * mm, "mid": v(92.96, -6.06) * mm, "end": v(95.61, -7.16) * mm});
            skArc(sketch, "E294", {"start": v(95.61, -7.16) * mm, "mid": v(98.26, -6.06) * mm, "end": v(99.36, -3.41) * mm});
            skArc(sketch, "E295", {"start": v(99.36, -3.41) * mm, "mid": v(98.26, -0.76) * mm, "end": v(95.61, 0.34) * mm});
            skArc(sketch, "E296", {"start": v(-102.82, -288.73) * mm, "mid": v(-105.47, -289.83) * mm, "end": v(-106.57, -292.48) * mm});
            skArc(sketch, "E297", {"start": v(-106.57, -292.48) * mm, "mid": v(-105.47, -295.13) * mm, "end": v(-102.82, -296.23) * mm});
            skArc(sketch, "E298", {"start": v(-102.82, -296.23) * mm, "mid": v(-100.17, -295.13) * mm, "end": v(-99.07, -292.48) * mm});
            skArc(sketch, "E299", {"start": v(-99.07, -292.48) * mm, "mid": v(-100.17, -289.83) * mm, "end": v(-102.82, -288.73) * mm});
            skArc(sketch, "E300", {"start": v(95.61, -581) * mm, "mid": v(92.96, -582.1) * mm, "end": v(91.86, -584.75) * mm});
            skArc(sketch, "E301", {"start": v(91.86, -584.75) * mm, "mid": v(92.96, -587.4) * mm, "end": v(95.61, -588.5) * mm});
            skArc(sketch, "E302", {"start": v(95.61, -588.5) * mm, "mid": v(98.26, -587.4) * mm, "end": v(99.36, -584.75) * mm});
            skArc(sketch, "E303", {"start": v(99.36, -584.75) * mm, "mid": v(98.26, -582.1) * mm, "end": v(95.61, -581) * mm});
            skArc(sketch, "E304", {"start": v(-94.2, -876.23) * mm, "mid": v(-96.85, -877.33) * mm, "end": v(-97.95, -879.98) * mm});
            skArc(sketch, "E305", {"start": v(-97.95, -879.98) * mm, "mid": v(-96.85, -882.63) * mm, "end": v(-94.2, -883.73) * mm});
            skArc(sketch, "E306", {"start": v(-94.2, -883.73) * mm, "mid": v(-91.55, -882.63) * mm, "end": v(-90.45, -879.98) * mm});
            skArc(sketch, "E307", {"start": v(-90.45, -879.98) * mm, "mid": v(-91.55, -877.33) * mm, "end": v(-94.2, -876.23) * mm});
            skLineSegment(sketch, "E308", {"start": v(-600, -1200) * mm, "end": v(600, -1200) * mm});
            skLineSegment(sketch, "E309", {"start": v(600, -1200) * mm, "end": v(600, 1200) * mm});
            skLineSegment(sketch, "E310", {"start": v(600, 1200) * mm, "end": v(-600, 1200) * mm});
            skLineSegment(sketch, "E311", {"start": v(-600, 1200) * mm, "end": v(-600, -1200) * mm});
            skSolve(sketch);
        }
        {
            var Q0;
            Q0=makeQuery(id+"F0.imprint","IMPRINT",FACE,{"disambiguationData":[TD([[makeQuery(id+"F0.imprint","IMPRINT",EDGE,{"derivedFrom":sQuery(id+"F0.wireOp",EDGE,"E0")}),1.0]])]});
            extrude(context, id + "F1", {"entities" : qUnion([Q0]), "depth" : 18 * mm});
        }
        {
            var Q0;
            Q0=makeQuery(id+"F0.imprint","IMPRINT",FACE,{"disambiguationData":[TD([[makeQuery(id+"F0.imprint","IMPRINT",EDGE,{"derivedFrom":sQuery(id+"F0.wireOp",EDGE,"E28")}),1.0]])]});
            extrude(context, id + "F2", {"entities" : qUnion([Q0]), "depth" : 18 * mm});
        }
    });
